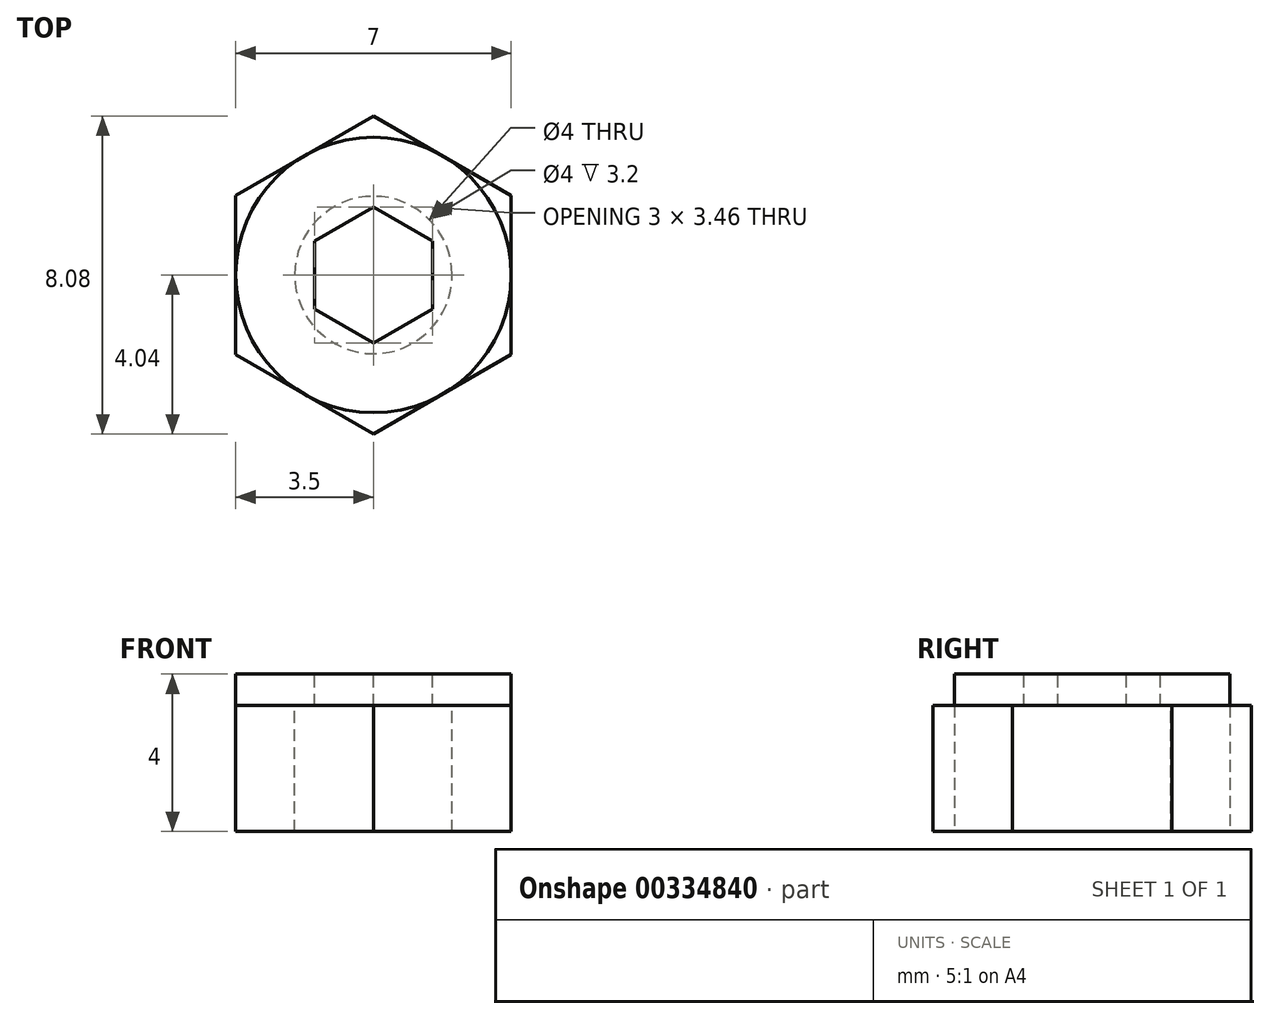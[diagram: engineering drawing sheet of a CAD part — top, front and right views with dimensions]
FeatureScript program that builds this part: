
annotation { "Feature Type Name" : "Feature", "Feature Type Description" : "" }
export const myFeature = defineFeature(function(context is Context, id is Id, definition is map)
    precondition{}
    {
        {
            var Q0;
            Q0=qCreatedBy(makeId("Top.planeOp"),FACE);
            var sketch = newSketch(context, id + "F0", { "sketchPlane" : qUnion([Q0])});
            skCircle(sketch, "E0", {"center": v(0, 0) * mm, "radius": 3.5 * mm});
            skSolve(sketch);
        }
        {
            var Q0;
            Q0 = qSketchRegion(id + "F0", true);
            extrude(context, id + "F1", {"entities" : qUnion([Q0]), "depth" : 4 * mm});
        }
        {
            var Q0;
            Q0=makeQuery(id+"F1.opExtrude","CAP_FACE",FACE,{"disambiguationData":[OSD([sQuery(id+"F0.wireOp",EDGE,"E0")])],"isStart":false});
            var sketch = newSketch(context, id + "F2", { "sketchPlane" : qUnion([Q0])});
            skCircle(sketch, "E1.cCircle", {"center": v(0, 0) * mm, "radius": 1.5 * mm, "construction": true});
            skLineSegment(sketch, "E1.0", {"start": v(0, 1.73) * mm, "end": v(1.5, 0.87) * mm});
            skLineSegment(sketch, "E1.1", {"start": v(1.5, 0.87) * mm, "end": v(1.5, -0.87) * mm});
            skLineSegment(sketch, "E1.2", {"start": v(1.5, -0.87) * mm, "end": v(0, -1.73) * mm});
            skLineSegment(sketch, "E1.3", {"start": v(0, -1.73) * mm, "end": v(-1.5, -0.87) * mm});
            skLineSegment(sketch, "E1.4", {"start": v(-1.5, -0.87) * mm, "end": v(-1.5, 0.87) * mm});
            skLineSegment(sketch, "E1.5", {"start": v(-1.5, 0.87) * mm, "end": v(0, 1.73) * mm});
            skPoint(sketch, "E1.0.midPoint", {"position": v(0.75, 1.3) * mm});
            skSolve(sketch);
        }
        {
            var Q0;
            Q0 = qSketchRegion(id + "F2", true);
            extrude(context, id + "F3", {"entities" : qUnion([Q0]), "operationType" : NewBodyOperationType.REMOVE, "oppositeDirection" : true, "depth" : 1.5 * mm});
        }
        {
            var Q0;
            Q0=makeQuery(id+"F1.opExtrude","CAP_FACE",FACE,{"disambiguationData":[OSD([sQuery(id+"F0.wireOp",EDGE,"E0")])],"isStart":true});
            var sketch = newSketch(context, id + "F4", { "sketchPlane" : qUnion([Q0])});
            skCircle(sketch, "E2", {"center": v(0, 0) * mm, "radius": 2 * mm});
            skSolve(sketch);
        }
        {
            var Q0;
            Q0 = qSketchRegion(id + "F4", true);
            extrude(context, id + "F5", {"entities" : qUnion([Q0]), "operationType" : NewBodyOperationType.ADD, "depth" : 20 * mm});
        }
        {
            var Q0;
            Q0=qCreatedBy(makeId("Top.planeOp"),FACE);
            var sketch = newSketch(context, id + "F6", { "sketchPlane" : qUnion([Q0])});
            skCircle(sketch, "E3.cCircle", {"center": v(0, 0) * mm, "radius": 3.5 * mm, "construction": true});
            skLineSegment(sketch, "E3.0", {"start": v(0, 4.04) * mm, "end": v(3.5, 2.02) * mm});
            skLineSegment(sketch, "E3.1", {"start": v(3.5, 2.02) * mm, "end": v(3.5, -2.02) * mm});
            skLineSegment(sketch, "E3.2", {"start": v(3.5, -2.02) * mm, "end": v(0, -4.04) * mm});
            skLineSegment(sketch, "E3.3", {"start": v(0, -4.04) * mm, "end": v(-3.5, -2.02) * mm});
            skLineSegment(sketch, "E3.4", {"start": v(-3.5, -2.02) * mm, "end": v(-3.5, 2.02) * mm});
            skLineSegment(sketch, "E3.5", {"start": v(-3.5, 2.02) * mm, "end": v(0, 4.04) * mm});
            skPoint(sketch, "E3.0.midPoint", {"position": v(1.75, 3.03) * mm});
            skSolve(sketch);
        }
        {
            var Q0;
            Q0 = qSketchRegion(id + "F6", true);
            extrude(context, id + "F7", {"entities" : qUnion([Q0]), "depth" : 3.2 * mm});
        }
        {
            var Q0;
            Q0=makeQuery(id+"F7.opExtrude","CAP_FACE",FACE,{"disambiguationData":[OSD([sQuery(id+"F6.wireOp",EDGE,"E3.0"),sQuery(id+"F6.wireOp",EDGE,"E3.1"),sQuery(id+"F6.wireOp",EDGE,"E3.2"),sQuery(id+"F6.wireOp",EDGE,"E3.3"),sQuery(id+"F6.wireOp",EDGE,"E3.4"),sQuery(id+"F6.wireOp",EDGE,"E3.5")])],"isStart":false});
            var sketch = newSketch(context, id + "F8", { "sketchPlane" : qUnion([Q0])});
            skCircle(sketch, "E4", {"center": v(0, 0) * mm, "radius": 2 * mm});
            skSolve(sketch);
        }
        {
            var Q0;
            Q0 = qSketchRegion(id + "F8", true);
            extrude(context, id + "F9", {"entities" : qUnion([Q0]), "operationType" : NewBodyOperationType.REMOVE, "oppositeDirection" : true, "depth" : 25 * mm});
        }
    });
